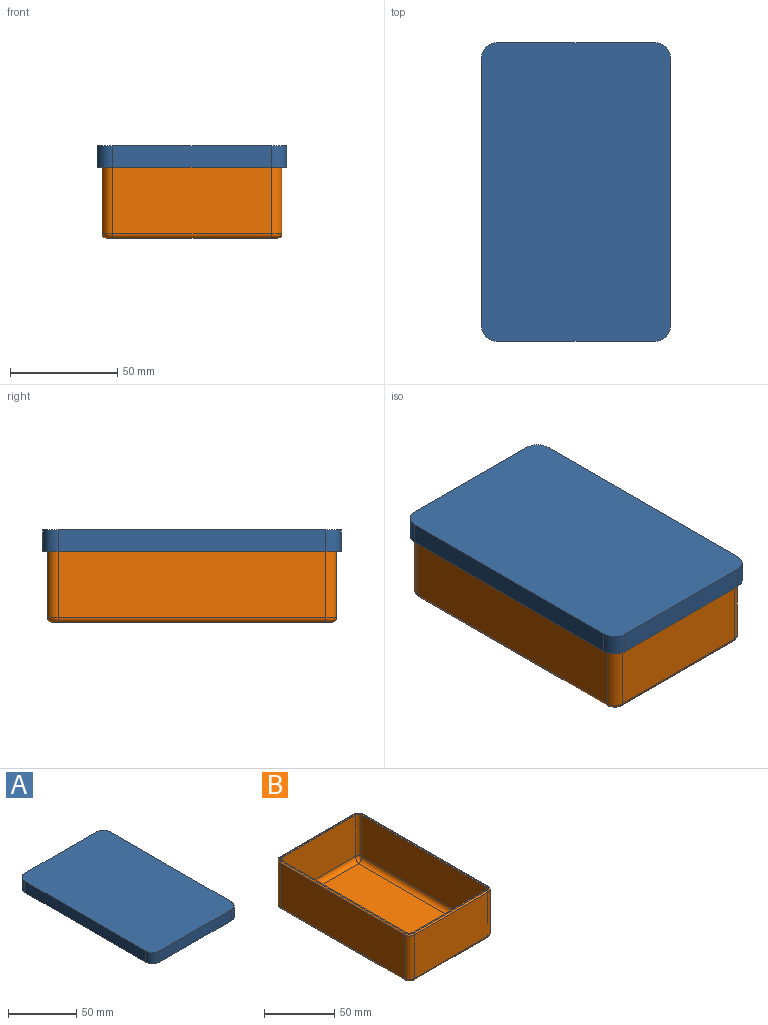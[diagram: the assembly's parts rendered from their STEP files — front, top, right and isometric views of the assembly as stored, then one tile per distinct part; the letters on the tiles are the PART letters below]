
ASSEMBLY  parts=2 mates=1
PART A: 27 faces, bbox 89x140x10 mm
  f0: plane 125x10mm, normal (-1,0,0), area 1250mm2, adj f1,f15,f16,f17
  f1: cylinder r=7.2mm len=10mm, axis (0,0,1), area 113.1mm2, adj f0,f2,f16,f17
  f2: plane 74x10mm, normal (0,-1,0), area 740mm2, adj f1,f3,f16,f17
  f3: cylinder r=7.2mm len=10mm, axis (0,0,1), area 113.1mm2, adj f2,f4,f16,f17
  f4: plane 125x10mm, normal (1,0,0), area 1250mm2, adj f3,f5,f16,f17
  f5: cylinder r=7.2mm len=10mm, axis (0,0,1), area 113.1mm2, adj f4,f6,f16,f17
  f6: plane 74x10mm, normal (0,1,0), area 740mm2, adj f5,f15,f16,f17
  f7: cylinder r=5.2mm len=7mm, axis (0,0,1), area 57.2mm2, adj f8,f14,f18,f21
  f8: plane 74x7mm, normal (0,-1,0), area 518mm2, adj f7,f9,f18,f23
  f9: cylinder r=5.2mm len=7mm, axis (0,0,1), area 57.2mm2, adj f8,f10,f18,f25
  f10: plane 125x7mm, normal (-1,0,0), area 875mm2, adj f9,f11,f18,f26
  f11: cylinder r=5.2mm len=7mm, axis (0,0,1), area 57.2mm2, adj f10,f12,f18,f24
  f12: plane 74x7mm, normal (0,1,0), area 518mm2, adj f11,f13,f18,f22
  f13: cylinder r=5.2mm len=7mm, axis (0,0,1), area 57.2mm2, adj f12,f14,f18,f20
  f14: plane 125x7mm, normal (1,0,0), area 875mm2, adj f7,f13,f18,f19
  f15: cylinder r=7.2mm len=10mm, axis (0,0,1), area 113.1mm2, adj f0,f6,f16,f17
  f16: plane 139.4x88.4mm, normal (0,0,-1), area 440.1mm2, adj f0,f1,f2,f3,f4,f5,f6,f15
  f17: plane 139.4x88.4mm, normal (0,0,1), area 12278.5mm2, adj f0,f1,f2,f3,f4,f5,f6,f15
  f18: plane 135.4x84.4mm, normal (0,0,-1), area 11404.5mm2, adj f7,f8,f9,f10,f11,f12,f13,f14
  f19: cylinder r=1mm len=125mm, axis (0,-1,0), area 196.3mm2, adj f14,f16,f20,f21
  f20: torus R=6.2mm, axis (0,0,1), area 13.7mm2, adj f13,f16,f19,f22
  f21: torus R=6.2mm, axis (0,0,1), area 13.7mm2, adj f7,f16,f19,f23
  f22: cylinder r=1mm len=74mm, axis (1,0,0), area 116.2mm2, adj f12,f16,f20,f24
  f23: cylinder r=1mm len=74mm, axis (-1,0,0), area 116.2mm2, adj f8,f16,f21,f25
  f24: torus R=6.2mm, axis (0,0,1), area 13.7mm2, adj f11,f16,f22,f26
  f25: torus R=6.2mm, axis (0,0,1), area 13.7mm2, adj f9,f16,f23,f26
  f26: cylinder r=1mm len=125mm, axis (0,1,0), area 196.3mm2, adj f10,f16,f24,f25
PART B: 43 faces, bbox 84.8x135.8x41 mm
  f0: plane 125x38mm, normal (1,0,0), area 4750mm2, adj f1,f7,f19,f35
  f1: cylinder r=5mm len=38mm, axis (0,0,-1), area 298.5mm2, adj f0,f2,f21,f37
  f2: plane 74x38mm, normal (0,1,0), area 2812mm2, adj f1,f3,f23,f39
  f3: cylinder r=5mm len=38mm, axis (0,0,-1), area 298.5mm2, adj f2,f4,f25,f41
  f4: plane 125x38mm, normal (-1,0,0), area 4750mm2, adj f3,f5,f26,f42
  f5: cylinder r=5mm len=38mm, axis (0,0,-1), area 298.5mm2, adj f4,f6,f24,f40
  f6: plane 74x38mm, normal (0,-1,0), area 2812mm2, adj f5,f7,f22,f38
  f7: cylinder r=5mm len=38mm, axis (0,0,-1), area 298.5mm2, adj f0,f6,f20,f36
  f8: plane 131x80mm, normal (0,0,-1), area 10472.3mm2, adj f35,f36,f37,f38,f39,f40,f41,f42
  f9: cylinder r=3mm len=36mm, axis (0,0,-1), area 169.6mm2, adj f10,f16,f17,f28
  f10: plane 74x36mm, normal (0,-1,0), area 2664mm2, adj f9,f11,f17,f30
  f11: cylinder r=3mm len=36mm, axis (0,0,-1), area 169.6mm2, adj f10,f12,f17,f32
  f12: plane 125x36mm, normal (-1,0,0), area 4500mm2, adj f11,f13,f17,f34
  f13: cylinder r=3mm len=36mm, axis (0,0,-1), area 169.6mm2, adj f12,f14,f17,f33
  f14: plane 74x36mm, normal (0,1,0), area 2664mm2, adj f13,f15,f17,f31
  f15: cylinder r=3mm len=36mm, axis (0,0,-1), area 169.6mm2, adj f14,f16,f17,f29
  f16: plane 125x36mm, normal (1,0,0), area 4500mm2, adj f9,f15,f17,f27
  f17: plane 133x82mm, normal (0,0,1), area 420mm2, adj f9,f10,f11,f12,f13,f14,f15,f16
  f18: plane 123x72mm, normal (0,0,1), area 8856mm2, adj f27,f30,f31,f34
  f19: cylinder r=1mm len=125mm, axis (0,-1,0), area 196.3mm2, adj f0,f17,f20,f21
  f20: torus R=4mm, axis (0,0,1), area 11.4mm2, adj f7,f17,f19,f22
  f21: torus R=4mm, axis (0,0,1), area 11.4mm2, adj f1,f17,f19,f23
  f22: cylinder r=1mm len=74mm, axis (-1,0,0), area 116.2mm2, adj f6,f17,f20,f24
  f23: cylinder r=1mm len=74mm, axis (1,0,0), area 116.2mm2, adj f2,f17,f21,f25
  f24: torus R=4mm, axis (0,0,1), area 11.4mm2, adj f5,f17,f22,f26
  f25: torus R=4mm, axis (0,0,1), area 11.4mm2, adj f3,f17,f23,f26
  f26: cylinder r=1mm len=125mm, axis (0,1,0), area 196.3mm2, adj f4,f17,f24,f25
  f27: cylinder r=4mm len=125mm, axis (0,-1,0), area 780.8mm2, adj f16,f18,f28,f29
  f28: bspline ~4.9x4mm, area 19.3mm2, adj f9,f27,f30
  f29: bspline ~4.9x4mm, area 19.3mm2, adj f15,f27,f31
  f30: cylinder r=4mm len=74mm, axis (-1,0,0), area 460.4mm2, adj f10,f18,f28,f32
  f31: cylinder r=4mm len=74mm, axis (1,0,0), area 460.4mm2, adj f14,f18,f29,f33
  f32: bspline ~4.9x4mm, area 19.3mm2, adj f11,f30,f34
  f33: bspline ~4.9x4mm, area 19.3mm2, adj f13,f31,f34
  f34: cylinder r=4mm len=125mm, axis (0,1,0), area 780.8mm2, adj f12,f18,f32,f33
  f35: cylinder r=2mm len=125mm, axis (0,1,0), area 392.7mm2, adj f0,f8,f36,f37
  f36: torus R=3mm, axis (0,0,1), area 21.1mm2, adj f7,f8,f35,f38
  f37: torus R=3mm, axis (0,0,1), area 21.1mm2, adj f1,f8,f35,f39
  f38: cylinder r=2mm len=74mm, axis (1,0,0), area 232.5mm2, adj f6,f8,f36,f40
  f39: cylinder r=2mm len=74mm, axis (-1,0,0), area 232.5mm2, adj f2,f8,f37,f41
  f40: torus R=3mm, axis (0,0,1), area 21.1mm2, adj f5,f8,f38,f42
  f41: torus R=3mm, axis (0,0,1), area 21.1mm2, adj f3,f8,f39,f42
  f42: cylinder r=2mm len=125mm, axis (0,-1,0), area 392.7mm2, adj f4,f8,f40,f41
PLACE A at identity
PLACE B t=(100,0,-43)mm
MATE planar B.f17 <-> A.f18  axis (0,0,1) through (142,67.5,-2)mm
